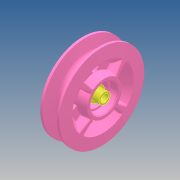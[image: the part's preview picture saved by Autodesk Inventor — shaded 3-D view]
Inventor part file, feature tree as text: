
AUTODESK INVENTOR PART (.ipt)
format: ipt  version: 2017 (Build 210142000, 142)  size: 933,376 bytes
history: native  units: mm
features: sketch x5, revolve x4, extrude x3, other x2, chamfer x2, plane x2, fillet x1, pattern_circular x1, projected_geometry x1
ambient origin geometry x8: Origin, YZ Plane, XZ Plane, XY Plane, X Axis, Y Axis, Z Axis, Center Point
bodies: Body1 (feature_tree), Body2 (feature_tree)
feature tree (21):
  other  "Sólido1"
  sketch  "Boceto1"  dims[d0=8.0mm d1=28.5mm]
  revolve  "Revolución1"  [1 undecoded]
  sketch  "Boceto2"  dims[d2=24.5mm d3=9.0mm]
  extrude  "Extrusión1"  Depth=9.0mm
  chamfer  "Chaflán1"  Distance=20.0mm
  extrude  "Extrusión2"  Depth=1.0mm
  extrude  "Extrusión3"  Depth=8.0mm
  chamfer  "Chaflán2"  Distance=3.0mm
  plane  "Plano de trabajo1"
  revolve  "Revolución3"  [1 undecoded]
  fillet  "Empalme1"  Radius=48.0mm
  plane  "Plano de trabajo2"
  revolve  "Revolución4"  [1 undecoded]
  pattern_circular  "Patrón circular1"  [2 undecoded]
  revolve  "Revolución2"  [1 undecoded]
  other  "espaciador"
  sketch  "Boceto3"  dims[d4=4.0mm]
  sketch  "Boceto4"  dims[d5=90.0mm d6=20.0mm d7=2.5mm]
  sketch  "Boceto5"  dims[d8=90.0deg d9=60.0mm d10=8.0mm d11=3.0mm d12=2.75mm d13=48.0mm d14=10.0mm d15=0.0mm d16=10.0mm d17=0.0mm d18=6.5mm d20=2.094395mm d21=60.0mm d22=4.0mm d23=3.0mm d24=45.0mm d25=45.0mm d26=8.0mm d27=12.0mm d28=16.0mm d29=8.0mm d30=90.0deg d31=20.0mm d32=32.0mm d33=22.0mm d34=6.368574mm d35=3.0mm d36=0.0mm d37=45.0deg d38=2.094395mm d39=1.5mm d40=40.0mm d41=360.0deg d43=22.5deg d44=2.0mm d45=2.094395mm d46=1.0mm d47=2.0mm d48=45.0deg d49=0.4mm d50=2.0mm d51=45.0deg]
  projected_geometry  "Contorno proyectado1"
note: 6 required parameter values undecoded (feature->parameter linkage not recoverable at this tier; creation-order binding heuristic only, values carry confidence <= 0.55)